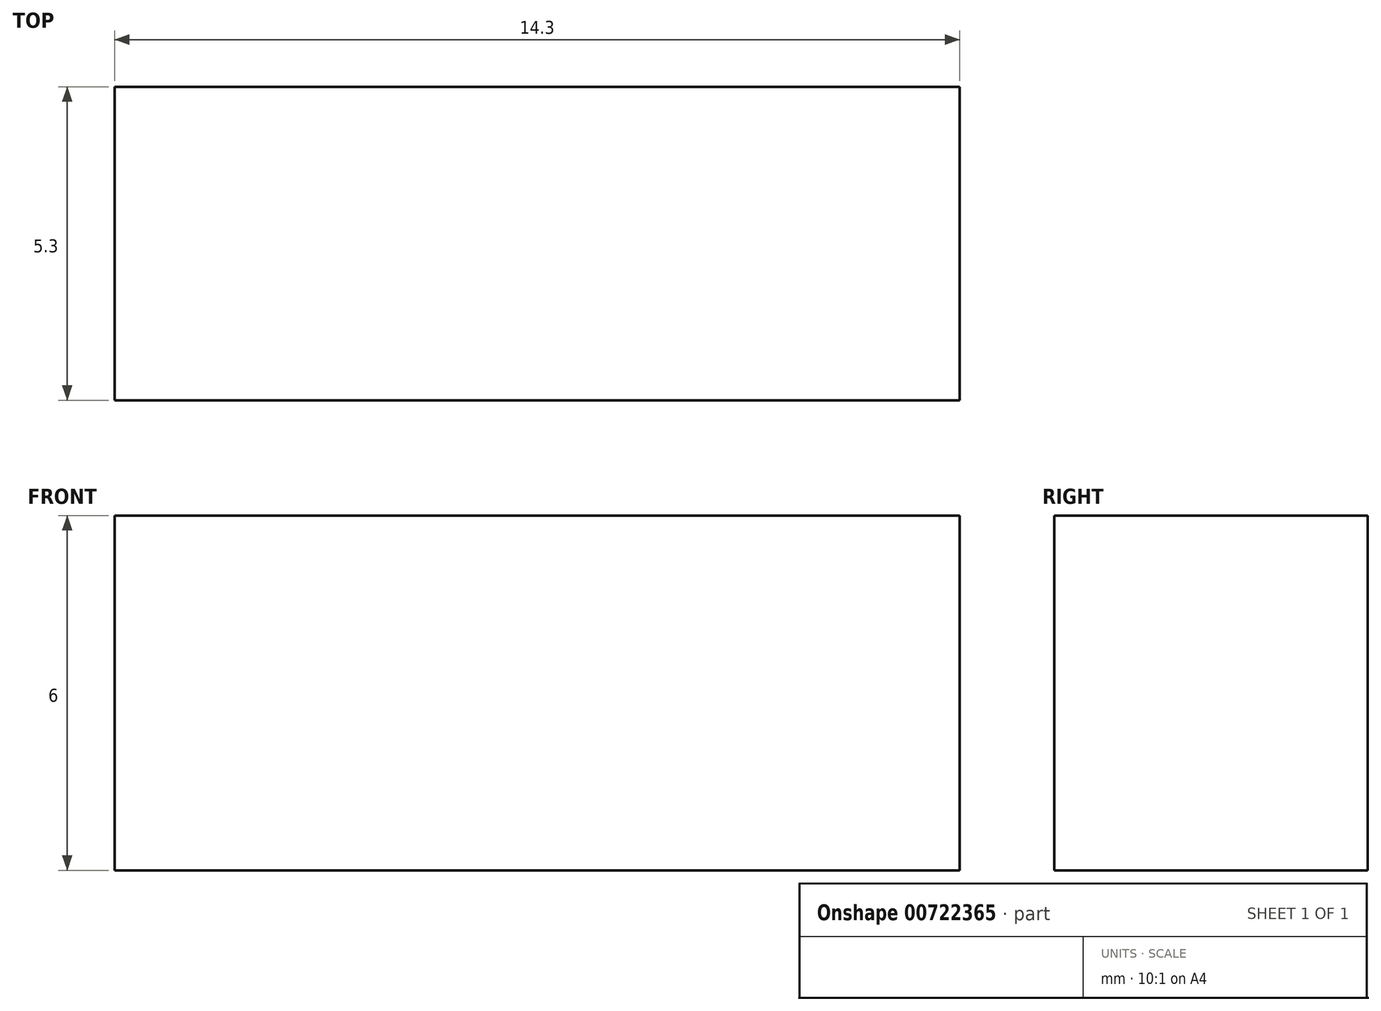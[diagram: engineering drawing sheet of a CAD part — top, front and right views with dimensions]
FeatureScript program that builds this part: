
annotation { "Feature Type Name" : "Feature", "Feature Type Description" : "" }
export const myFeature = defineFeature(function(context is Context, id is Id, definition is map)
    precondition{}
    {
        {
            var Q0;
            Q0=qCreatedBy(makeId("Top.planeOp"),FACE);
            var sketch = newSketch(context, id + "F0", { "sketchPlane" : qUnion([Q0])});
            skLineSegment(sketch, "E0.bottom", {"start": v(1.15, 0) * mm, "end": v(13.15, 0) * mm});
            skLineSegment(sketch, "E0.top", {"start": v(0, 6.8) * mm, "end": v(14.3, 6.8) * mm});
            skLineSegment(sketch, "E0.left", {"start": v(0, 1.5) * mm, "end": v(0, 6.8) * mm});
            skLineSegment(sketch, "E0.right", {"start": v(14.3, 1.5) * mm, "end": v(14.3, 6.8) * mm});
            skLineSegment(sketch, "E1.left", {"start": v(0, 6.8) * mm, "end": v(0, 1.5) * mm});
            skLineSegment(sketch, "E1.right", {"start": v(14.3, 6.8) * mm, "end": v(14.3, 1.5) * mm});
            skLineSegment(sketch, "E2.bottom", {"start": v(7.15, 0) * mm, "end": v(13.15, 0) * mm});
            skLineSegment(sketch, "E3.bottom", {"start": v(7.15, 0) * mm, "end": v(1.15, 0) * mm});
            skLineSegment(sketch, "E4", {"start": v(0, 1.5) * mm, "end": v(1.15, 0) * mm});
            skLineSegment(sketch, "E5", {"start": v(14.3, 1.5) * mm, "end": v(13.15, 0) * mm});
            skPoint(sketch, "E6.orphan", {"position": v(0, 0) * mm});
            skPoint(sketch, "E7.orphan", {"position": v(14.3, 0) * mm});
            skLineSegment(sketch, "E8", {"start": v(0, 1.5) * mm, "end": v(14.3, 1.5) * mm});
            skSolve(sketch);
        }
        {
            var Q0;
            Q0=makeQuery(id+"F0.imprint","IMPRINT",FACE,{"disambiguationData":[TD([[makeQuery(id+"F0.imprint","IMPRINT",EDGE,{"derivedFrom":sQuery(id+"F0.wireOp",EDGE,"E2.bottom")}),1.0]])]});
            var Q1;
            Q1=makeQuery(id+"F0.imprint","IMPRINT",FACE,{"disambiguationData":[TD([[makeQuery(id+"F0.imprint","IMPRINT",EDGE,{"derivedFrom":sQuery(id+"F0.wireOp",EDGE,"E0.top")}),-1.0]])]});
            extrude(context, id + "F1", {"entities" : qUnion([Q0, Q1]), "depth" : 6 * mm, "offsetDistance" : 25 * mm});
        }
    });
